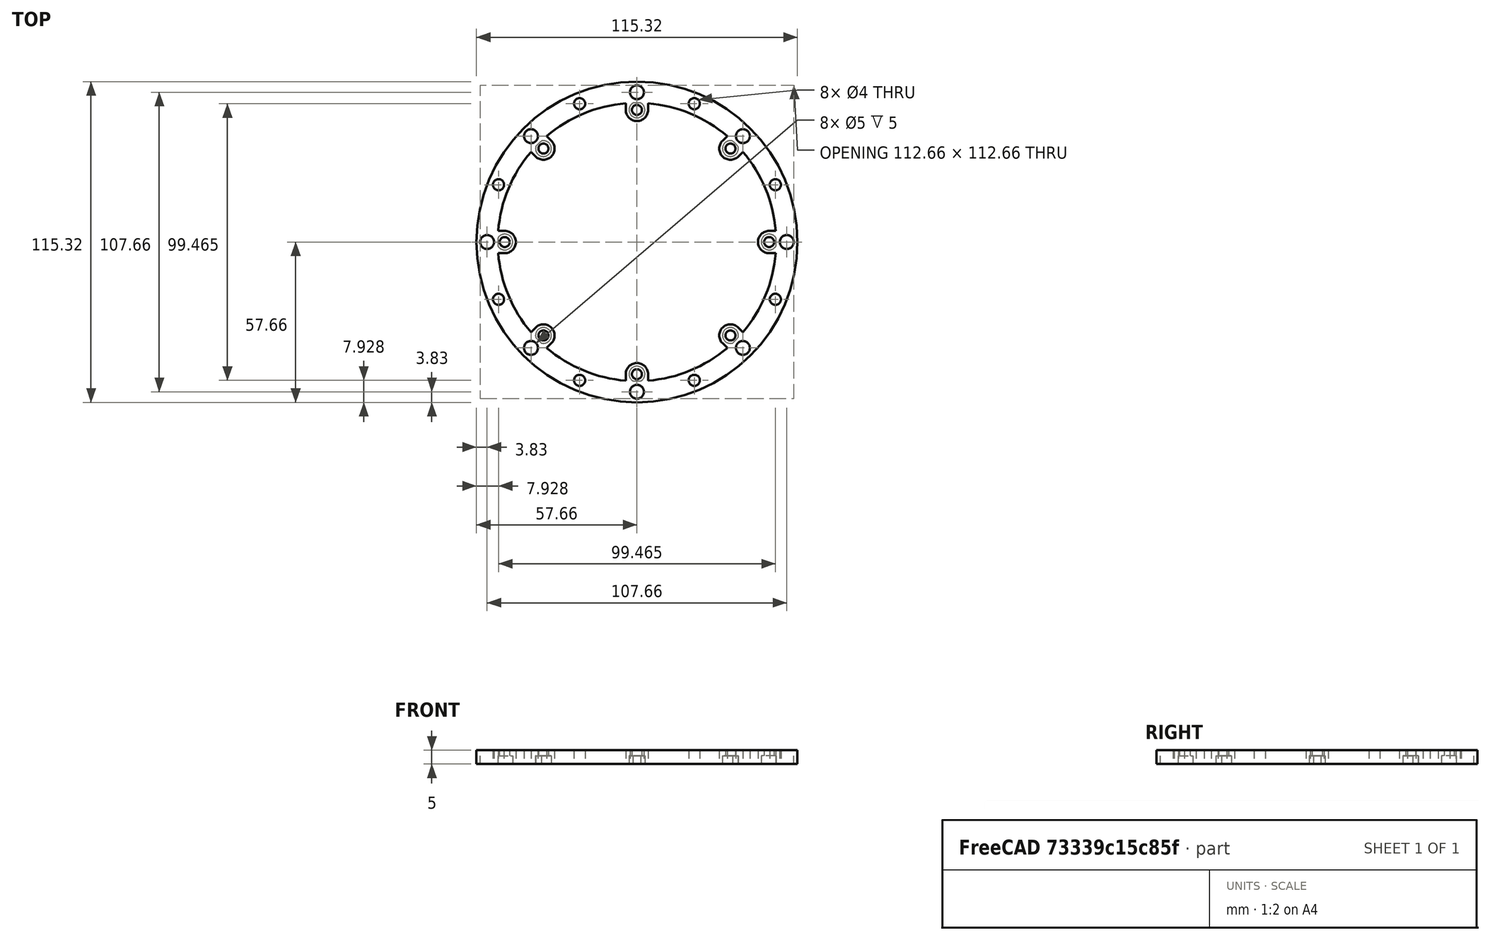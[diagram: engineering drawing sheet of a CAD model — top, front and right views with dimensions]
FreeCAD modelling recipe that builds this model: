
FCSTD DOCUMENT  (FreeCAD 0.20R)
Label: XL30ColumnAttachmentRing01
License: All rights reserved
LicenseURL: http://en.wikipedia.org/wiki/All_rights_reserved
objects: Part::Cylinder×34, TechDraw::DrawViewDimension×19, Part::Compound×18, Part::MultiFuse×17, Part::Cut×11, Part::Box×8, Part::FeaturePython×8, TechDraw::DrawProjGroupItem×2, Spreadsheet::Sheet×1, TechDraw::DrawSVGTemplate×1, TechDraw::DrawProjGroup×1, TechDraw::DrawViewSection×1, TechDraw::DrawViewAnnotation×1, TechDraw::DrawPage×1
note: 96 computed .brp shape members not serialized (recipe doc carries the construction recipe); baked Part::Feature solids carry a one-line shape summary decoded from their .brp

FEATURE [Spreadsheet::Sheet] Spreadsheet  label="AttachmentRing01"
  cells = A1=Ring configuration; A2=Inside diameter; B2(ring_id)=100; C2=Inside diameter of the column / poleshoe; E2=Ring width; F2(ring_width)==ring_od - ring_id; A3=Outside diameter; B3(ring_od)==100 + 2 * 7.66; C3=Outside diameter; A4=Thickness; B4(ring_thickness)=5; C4=Thickness of the mounting rin; A5=Thickness below mountscrew; B5(thickness_m3_below)=2
FEATURE [Part::Cylinder] Cylinder
  Angle = 360
  AttacherType = Attacher::AttachEngine3D
  FirstAngle = 0
  Height = 5
  Radius = 57.66
  SecondAngle = 0
  expr: Height = <<AttachmentRing01>>.ring_thickness
  expr: Radius = <<AttachmentRing01>>.ring_od / 2
FEATURE [Part::Cylinder] Cylinder001
  Angle = 360
  AttacherType = Attacher::AttachEngine3D
  FirstAngle = 0
  Height = 5
  Radius = 50
  SecondAngle = 0
  expr: Height = <<AttachmentRing01>>.ring_thickness
  expr: Radius = <<AttachmentRing01>>.ring_id / 2
FEATURE [Part::Cut] Cut
  Base = -> Cylinder
  Tool = -> Cylinder001
FEATURE [Part::Box] Box007  label="Cube007"
  AttacherType = Attacher::AttachEngine3D
  Height = 5
  Length = 4
  Placement = pos=(47.5,-4,0) rot=(0,0,1;0rad)
  Width = 8
  expr: Height = <<AttachmentRing01>>.ring_thickness
FEATURE [Part::Cylinder] Cylinder009
  Angle = 360
  AttacherType = Attacher::AttachEngine3D
  FirstAngle = 0
  Height = 5
  Placement = pos=(47.5,0,0) rot=(0,0,1;0rad)
  Radius = 4
  SecondAngle = 0
  expr: Height = <<AttachmentRing01>>.ring_thickness
FEATURE [Part::MultiFuse] Fusion008
  Shapes = -> [Cylinder009,Box007]
FEATURE [Part::Cylinder] Cylinder011
  Angle = 360
  AttacherType = Attacher::AttachEngine3D
  FirstAngle = 0
  Height = 10
  Placement = pos=(47.5,0,0) rot=(0,0,1;0rad)
  Radius = 1.8
  SecondAngle = 0
FEATURE [Part::Cylinder] Cylinder012
  Angle = 360
  AttacherType = Attacher::AttachEngine3D
  FirstAngle = 0
  Height = 3
  Placement = pos=(47.5,0,0) rot=(0,0,1;0rad)
  Radius = 2.84
  SecondAngle = 0
  expr: Height = <<AttachmentRing01>>.ring_thickness - <<AttachmentRing01>>.thickness_m3_below
FEATURE [Part::MultiFuse] Fusion
  Shapes = -> [Cylinder012,Cylinder011]
FEATURE [Part::Cut] Cut001
  Base = -> Fusion008
  Tool = -> Fusion
FEATURE [Part::Box] Box008  label="Cube008"
  AttacherType = Attacher::AttachEngine3D
  Height = 5
  Length = 4
  Placement = pos=(47.5,-4,0) rot=(0,0,1;0rad)
  Width = 8
  expr: Height = <<AttachmentRing01>>.ring_thickness
FEATURE [Part::Cylinder] Cylinder013
  Angle = 360
  AttacherType = Attacher::AttachEngine3D
  FirstAngle = 0
  Height = 5
  Placement = pos=(47.5,0,0) rot=(0,0,1;0rad)
  Radius = 4
  SecondAngle = 0
  expr: Height = <<AttachmentRing01>>.ring_thickness
FEATURE [Part::Cylinder] Cylinder014
  Angle = 360
  AttacherType = Attacher::AttachEngine3D
  FirstAngle = 0
  Height = 10
  Placement = pos=(47.5,0,0) rot=(0,0,1;0rad)
  Radius = 1.8
  SecondAngle = 0
FEATURE [Part::Cylinder] Cylinder015
  Angle = 360
  AttacherType = Attacher::AttachEngine3D
  FirstAngle = 0
  Height = 3
  Placement = pos=(47.5,0,0) rot=(0,0,1;0rad)
  Radius = 2.84
  SecondAngle = 0
  expr: Height = <<AttachmentRing01>>.ring_thickness - <<AttachmentRing01>>.thickness_m3_below
FEATURE [Part::MultiFuse] Fusion009
  Shapes = -> [Cylinder015,Cylinder014]
FEATURE [Part::MultiFuse] Fusion010
  Shapes = -> [Cylinder013,Box008]
FEATURE [Part::Cut] Cut002
  Base = -> Fusion010
  Placement = pos=(0,0,0) rot=(0,0,1;0.785398rad)
  Tool = -> Fusion009
FEATURE [Part::Box] Box009  label="Cube009"
  AttacherType = Attacher::AttachEngine3D
  Height = 5
  Length = 4
  Placement = pos=(47.5,-4,0) rot=(0,0,1;0rad)
  Width = 8
  expr: Height = <<AttachmentRing01>>.ring_thickness
FEATURE [Part::Cylinder] Cylinder016
  Angle = 360
  AttacherType = Attacher::AttachEngine3D
  FirstAngle = 0
  Height = 5
  Placement = pos=(47.5,0,0) rot=(0,0,1;0rad)
  Radius = 4
  SecondAngle = 0
  expr: Height = <<AttachmentRing01>>.ring_thickness
FEATURE [Part::Cylinder] Cylinder017
  Angle = 360
  AttacherType = Attacher::AttachEngine3D
  FirstAngle = 0
  Height = 10
  Placement = pos=(47.5,0,0) rot=(0,0,1;0rad)
  Radius = 1.8
  SecondAngle = 0
FEATURE [Part::Cylinder] Cylinder018
  Angle = 360
  AttacherType = Attacher::AttachEngine3D
  FirstAngle = 0
  Height = 3
  Placement = pos=(47.5,0,0) rot=(0,0,1;0rad)
  Radius = 2.84
  SecondAngle = 0
  expr: Height = <<AttachmentRing01>>.ring_thickness - <<AttachmentRing01>>.thickness_m3_below
FEATURE [Part::MultiFuse] Fusion011
  Shapes = -> [Cylinder018,Cylinder017]
FEATURE [Part::MultiFuse] Fusion012
  Shapes = -> [Cylinder016,Box009]
FEATURE [Part::Cut] Cut003
  Base = -> Fusion012
  Placement = pos=(0,0,0) rot=(0,0,1;1.5708rad)
  Tool = -> Fusion011
FEATURE [Part::Box] Box010  label="Cube010"
  AttacherType = Attacher::AttachEngine3D
  Height = 5
  Length = 4
  Placement = pos=(47.5,-4,0) rot=(0,0,1;0rad)
  Width = 8
  expr: Height = <<AttachmentRing01>>.ring_thickness
FEATURE [Part::Cylinder] Cylinder019
  Angle = 360
  AttacherType = Attacher::AttachEngine3D
  FirstAngle = 0
  Height = 5
  Placement = pos=(47.5,0,0) rot=(0,0,1;0rad)
  Radius = 4
  SecondAngle = 0
  expr: Height = <<AttachmentRing01>>.ring_thickness
FEATURE [Part::Cylinder] Cylinder020
  Angle = 360
  AttacherType = Attacher::AttachEngine3D
  FirstAngle = 0
  Height = 10
  Placement = pos=(47.5,0,0) rot=(0,0,1;0rad)
  Radius = 1.8
  SecondAngle = 0
FEATURE [Part::Cylinder] Cylinder021
  Angle = 360
  AttacherType = Attacher::AttachEngine3D
  FirstAngle = 0
  Height = 3
  Placement = pos=(47.5,0,0) rot=(0,0,1;0rad)
  Radius = 2.84
  SecondAngle = 0
  expr: Height = <<AttachmentRing01>>.ring_thickness - <<AttachmentRing01>>.thickness_m3_below
FEATURE [Part::MultiFuse] Fusion013
  Shapes = -> [Cylinder021,Cylinder020]
FEATURE [Part::MultiFuse] Fusion014
  Shapes = -> [Cylinder019,Box010]
FEATURE [Part::Cut] Cut004
  Base = -> Fusion014
  Placement = pos=(0,0,0) rot=(0,0,1;2.35619rad)
  Tool = -> Fusion013
FEATURE [Part::Box] Box011  label="Cube011"
  AttacherType = Attacher::AttachEngine3D
  Height = 5
  Length = 4
  Placement = pos=(47.5,-4,0) rot=(0,0,1;0rad)
  Width = 8
  expr: Height = <<AttachmentRing01>>.ring_thickness
FEATURE [Part::Cylinder] Cylinder022
  Angle = 360
  AttacherType = Attacher::AttachEngine3D
  FirstAngle = 0
  Height = 5
  Placement = pos=(47.5,0,0) rot=(0,0,1;0rad)
  Radius = 4
  SecondAngle = 0
  expr: Height = <<AttachmentRing01>>.ring_thickness
FEATURE [Part::Cylinder] Cylinder023
  Angle = 360
  AttacherType = Attacher::AttachEngine3D
  FirstAngle = 0
  Height = 10
  Placement = pos=(47.5,0,0) rot=(0,0,1;0rad)
  Radius = 1.8
  SecondAngle = 0
FEATURE [Part::Cylinder] Cylinder024
  Angle = 360
  AttacherType = Attacher::AttachEngine3D
  FirstAngle = 0
  Height = 3
  Placement = pos=(47.5,0,0) rot=(0,0,1;0rad)
  Radius = 2.84
  SecondAngle = 0
  expr: Height = <<AttachmentRing01>>.ring_thickness - <<AttachmentRing01>>.thickness_m3_below
FEATURE [Part::MultiFuse] Fusion015
  Shapes = -> [Cylinder024,Cylinder023]
FEATURE [Part::MultiFuse] Fusion016
  Shapes = -> [Cylinder022,Box011]
FEATURE [Part::Cut] Cut005
  Base = -> Fusion016
  Placement = pos=(0,0,0) rot=(0,0,1;3.14159rad)
  Tool = -> Fusion015
FEATURE [Part::Box] Box012  label="Cube012"
  AttacherType = Attacher::AttachEngine3D
  Height = 5
  Length = 4
  Placement = pos=(47.5,-4,0) rot=(0,0,1;0rad)
  Width = 8
  expr: Height = <<AttachmentRing01>>.ring_thickness
FEATURE [Part::Cylinder] Cylinder025
  Angle = 360
  AttacherType = Attacher::AttachEngine3D
  FirstAngle = 0
  Height = 5
  Placement = pos=(47.5,0,0) rot=(0,0,1;0rad)
  Radius = 4
  SecondAngle = 0
  expr: Height = <<AttachmentRing01>>.ring_thickness
FEATURE [Part::Cylinder] Cylinder026
  Angle = 360
  AttacherType = Attacher::AttachEngine3D
  FirstAngle = 0
  Height = 10
  Placement = pos=(47.5,0,0) rot=(0,0,1;0rad)
  Radius = 1.8
  SecondAngle = 0
FEATURE [Part::Cylinder] Cylinder027
  Angle = 360
  AttacherType = Attacher::AttachEngine3D
  FirstAngle = 0
  Height = 3
  Placement = pos=(47.5,0,0) rot=(0,0,1;0rad)
  Radius = 2.84
  SecondAngle = 0
  expr: Height = <<AttachmentRing01>>.ring_thickness - <<AttachmentRing01>>.thickness_m3_below
FEATURE [Part::MultiFuse] Fusion017
  Shapes = -> [Cylinder027,Cylinder026]
FEATURE [Part::MultiFuse] Fusion018
  Shapes = -> [Cylinder025,Box012]
FEATURE [Part::Cut] Cut006
  Base = -> Fusion018
  Placement = pos=(0,0,0) rot=(0,0,1;3.92699rad)
  Tool = -> Fusion017
FEATURE [Part::Box] Box013  label="Cube013"
  AttacherType = Attacher::AttachEngine3D
  Height = 5
  Length = 4
  Placement = pos=(47.5,-4,0) rot=(0,0,1;0rad)
  Width = 8
  expr: Height = <<AttachmentRing01>>.ring_thickness
FEATURE [Part::Cylinder] Cylinder028
  Angle = 360
  AttacherType = Attacher::AttachEngine3D
  FirstAngle = 0
  Height = 5
  Placement = pos=(47.5,0,0) rot=(0,0,1;0rad)
  Radius = 4
  SecondAngle = 0
  expr: Height = <<AttachmentRing01>>.ring_thickness
FEATURE [Part::Cylinder] Cylinder029
  Angle = 360
  AttacherType = Attacher::AttachEngine3D
  FirstAngle = 0
  Height = 10
  Placement = pos=(47.5,0,0) rot=(0,0,1;0rad)
  Radius = 1.8
  SecondAngle = 0
FEATURE [Part::Cylinder] Cylinder030
  Angle = 360
  AttacherType = Attacher::AttachEngine3D
  FirstAngle = 0
  Height = 3
  Placement = pos=(47.5,0,0) rot=(0,0,1;0rad)
  Radius = 2.84
  SecondAngle = 0
  expr: Height = <<AttachmentRing01>>.ring_thickness - <<AttachmentRing01>>.thickness_m3_below
FEATURE [Part::MultiFuse] Fusion019
  Shapes = -> [Cylinder030,Cylinder029]
FEATURE [Part::MultiFuse] Fusion020
  Shapes = -> [Cylinder028,Box013]
FEATURE [Part::Cut] Cut007
  Base = -> Fusion020
  Placement = pos=(0,0,0) rot=(0,0,1;4.71239rad)
  Tool = -> Fusion019
FEATURE [Part::Box] Box014  label="Cube014"
  AttacherType = Attacher::AttachEngine3D
  Height = 5
  Length = 4
  Placement = pos=(47.5,-4,0) rot=(0,0,1;0rad)
  Width = 8
  expr: Height = <<AttachmentRing01>>.ring_thickness
FEATURE [Part::Cylinder] Cylinder031
  Angle = 360
  AttacherType = Attacher::AttachEngine3D
  FirstAngle = 0
  Height = 5
  Placement = pos=(47.5,0,0) rot=(0,0,1;0rad)
  Radius = 4
  SecondAngle = 0
  expr: Height = <<AttachmentRing01>>.ring_thickness
FEATURE [Part::Cylinder] Cylinder032
  Angle = 360
  AttacherType = Attacher::AttachEngine3D
  FirstAngle = 0
  Height = 10
  Placement = pos=(47.5,0,0) rot=(0,0,1;0rad)
  Radius = 1.8
  SecondAngle = 0
FEATURE [Part::Cylinder] Cylinder033
  Angle = 360
  AttacherType = Attacher::AttachEngine3D
  FirstAngle = 0
  Height = 3
  Placement = pos=(47.5,0,0) rot=(0,0,1;0rad)
  Radius = 2.84
  SecondAngle = 0
  expr: Height = <<AttachmentRing01>>.ring_thickness - <<AttachmentRing01>>.thickness_m3_below
FEATURE [Part::MultiFuse] Fusion021
  Shapes = -> [Cylinder033,Cylinder032]
FEATURE [Part::MultiFuse] Fusion022
  Shapes = -> [Cylinder031,Box014]
FEATURE [Part::Cut] Cut008
  Base = -> Fusion022
  Placement = pos=(0,0,0) rot=(0,0,1;5.49779rad)
  Tool = -> Fusion021
FEATURE [Part::MultiFuse] Fusion023
  Shapes = -> [Cut,Cut001,Cut002,Cut003,Cut004,Cut005,Cut006,Cut007,Cut008]
FEATURE [Part::FeaturePython] Screw  label="M4x7-Screw001"  # Fasteners workbench fastener (typed FeaturePython)
  Placement = pos=(53.83,0,3.82) rot=(0,0,1;0rad)
  diameter = 5
  invert = false
  leftHanded = false
  length = 11
  lengthCustom = 7
  matchOuter = false
  offset = 0
  thread = false
  type = 48
  expr: .Placement.Base.x = (<<AttachmentRing01>>.ring_od + <<AttachmentRing01>>.ring_id) / 4
  expr: lengthCustom = <<AttachmentRing01>>.ring_thickness + 2
FEATURE [Part::Compound] Compound
  Links = -> [Screw]
  Placement = pos=(0,0,0) rot=(0,0,1;0.392699rad)
FEATURE [Part::FeaturePython] Screw001  label="M4x7-Screw002"  # Fasteners workbench fastener (typed FeaturePython)
  Placement = pos=(53.83,0,3.82) rot=(0,0,1;0rad)
  diameter = 5
  invert = false
  leftHanded = false
  length = 11
  lengthCustom = 7
  matchOuter = false
  offset = 0
  thread = false
  type = 48
  expr: .Placement.Base.x = (<<AttachmentRing01>>.ring_od + <<AttachmentRing01>>.ring_id) / 4
  expr: lengthCustom = <<AttachmentRing01>>.ring_thickness + 2
FEATURE [Part::Compound] Compound001
  Links = -> [Screw001]
  Placement = pos=(0,0,0) rot=(0,0,1;1.1781rad)
FEATURE [Part::FeaturePython] Screw002  label="M4x7-Screw003"  # Fasteners workbench fastener (typed FeaturePython)
  Placement = pos=(53.83,0,3.82) rot=(0,0,1;0rad)
  diameter = 5
  invert = false
  leftHanded = false
  length = 11
  lengthCustom = 7
  matchOuter = false
  offset = 0
  thread = false
  type = 48
  expr: .Placement.Base.x = (<<AttachmentRing01>>.ring_od + <<AttachmentRing01>>.ring_id) / 4
  expr: lengthCustom = <<AttachmentRing01>>.ring_thickness + 2
FEATURE [Part::Compound] Compound002
  Links = -> [Screw002]
  Placement = pos=(0,0,0) rot=(0,0,1;1.96349rad)
FEATURE [Part::FeaturePython] Screw003  label="M4x7-Screw004"  # Fasteners workbench fastener (typed FeaturePython)
  Placement = pos=(53.83,0,3.82) rot=(0,0,1;0rad)
  diameter = 5
  invert = false
  leftHanded = false
  length = 11
  lengthCustom = 7
  matchOuter = false
  offset = 0
  thread = false
  type = 48
  expr: .Placement.Base.x = (<<AttachmentRing01>>.ring_od + <<AttachmentRing01>>.ring_id) / 4
  expr: lengthCustom = <<AttachmentRing01>>.ring_thickness + 2
FEATURE [Part::Compound] Compound003
  Links = -> [Screw003]
  Placement = pos=(0,0,0) rot=(0,0,1;2.74889rad)
FEATURE [Part::FeaturePython] Screw004  label="M4x7-Screw005"  # Fasteners workbench fastener (typed FeaturePython)
  Placement = pos=(53.83,0,3.82) rot=(0,0,1;0rad)
  diameter = 5
  invert = false
  leftHanded = false
  length = 11
  lengthCustom = 7
  matchOuter = false
  offset = 0
  thread = false
  type = 48
  expr: .Placement.Base.x = (<<AttachmentRing01>>.ring_od + <<AttachmentRing01>>.ring_id) / 4
  expr: lengthCustom = <<AttachmentRing01>>.ring_thickness + 2
FEATURE [Part::Compound] Compound004
  Links = -> [Screw004]
  Placement = pos=(0,0,0) rot=(0,0,1;3.53429rad)
FEATURE [Part::FeaturePython] Screw005  label="M4x7-Screw006"  # Fasteners workbench fastener (typed FeaturePython)
  Placement = pos=(53.83,0,3.82) rot=(0,0,1;0rad)
  diameter = 5
  invert = false
  leftHanded = false
  length = 11
  lengthCustom = 7
  matchOuter = false
  offset = 0
  thread = false
  type = 48
  expr: .Placement.Base.x = (<<AttachmentRing01>>.ring_od + <<AttachmentRing01>>.ring_id) / 4
  expr: lengthCustom = <<AttachmentRing01>>.ring_thickness + 2
FEATURE [Part::Compound] Compound005
  Links = -> [Screw005]
  Placement = pos=(0,0,0) rot=(0,0,1;4.31969rad)
FEATURE [Part::FeaturePython] Screw006  label="M4x7-Screw007"  # Fasteners workbench fastener (typed FeaturePython)
  Placement = pos=(53.83,0,3.82) rot=(0,0,1;0rad)
  diameter = 5
  invert = false
  leftHanded = false
  length = 11
  lengthCustom = 7
  matchOuter = false
  offset = 0
  thread = false
  type = 48
  expr: .Placement.Base.x = (<<AttachmentRing01>>.ring_od + <<AttachmentRing01>>.ring_id) / 4
  expr: lengthCustom = <<AttachmentRing01>>.ring_thickness + 2
FEATURE [Part::Compound] Compound006
  Links = -> [Screw006]
  Placement = pos=(0,0,0) rot=(0,0,1;5.10509rad)
FEATURE [Part::FeaturePython] Screw007  label="M4x7-Screw"  # Fasteners workbench fastener (typed FeaturePython)
  Placement = pos=(53.83,0,3.82) rot=(0,0,1;0rad)
  diameter = 5
  invert = false
  leftHanded = false
  length = 11
  lengthCustom = 7
  matchOuter = false
  offset = 0
  thread = false
  type = 48
  expr: .Placement.Base.x = (<<AttachmentRing01>>.ring_od + <<AttachmentRing01>>.ring_id) / 4
  expr: lengthCustom = <<AttachmentRing01>>.ring_thickness + 2
FEATURE [Part::Compound] Compound007
  Links = -> [Screw007]
  Placement = pos=(0,0,0) rot=(0,0,1;5.89049rad)
FEATURE [Part::Compound] Compound008  label="M4Threadsx8"
  Links = -> [Compound007,Compound,Compound001,Compound002,Compound003,Compound004,Compound005,Compound006]
  Placement = pos=(0,0,2) rot=(0,0,1;0rad)
FEATURE [Part::Cut] Cut009
  Base = -> Fusion023
  Tool = -> Compound008
FEATURE [Part::Cylinder] Cylinder035
  Angle = 360
  AttacherType = Attacher::AttachEngine3D
  FirstAngle = 0
  Height = 5
  Placement = pos=(53.83,0,0) rot=(0,0,1;0rad)
  Radius = 2.5
  SecondAngle = 0
  expr: .Placement.Base.x = (<<AttachmentRing01>>.ring_od + <<AttachmentRing01>>.ring_id) / 4
  expr: Height = <<AttachmentRing01>>.ring_thickness
FEATURE [Part::Compound] Compound009
  Links = -> [Cylinder035]
FEATURE [Part::Cylinder] Cylinder036
  Angle = 360
  AttacherType = Attacher::AttachEngine3D
  FirstAngle = 0
  Height = 5
  Placement = pos=(53.83,0,0) rot=(0,0,1;0rad)
  Radius = 2.5
  SecondAngle = 0
  expr: .Placement.Base.x = (<<AttachmentRing01>>.ring_od + <<AttachmentRing01>>.ring_id) / 4
  expr: Height = <<AttachmentRing01>>.ring_thickness
FEATURE [Part::Compound] Compound010
  Links = -> [Cylinder036]
  Placement = pos=(0,0,0) rot=(0,0,1;0.785398rad)
FEATURE [Part::Cylinder] Cylinder037
  Angle = 360
  AttacherType = Attacher::AttachEngine3D
  FirstAngle = 0
  Height = 5
  Placement = pos=(53.83,0,0) rot=(0,0,1;0rad)
  Radius = 2.5
  SecondAngle = 0
  expr: .Placement.Base.x = (<<AttachmentRing01>>.ring_od + <<AttachmentRing01>>.ring_id) / 4
  expr: Height = <<AttachmentRing01>>.ring_thickness
FEATURE [Part::Compound] Compound011
  Links = -> [Cylinder037]
  Placement = pos=(0,0,0) rot=(0,0,1;1.5708rad)
FEATURE [Part::Cylinder] Cylinder038
  Angle = 360
  AttacherType = Attacher::AttachEngine3D
  FirstAngle = 0
  Height = 5
  Placement = pos=(53.83,0,0) rot=(0,0,1;0rad)
  Radius = 2.5
  SecondAngle = 0
  expr: .Placement.Base.x = (<<AttachmentRing01>>.ring_od + <<AttachmentRing01>>.ring_id) / 4
  expr: Height = <<AttachmentRing01>>.ring_thickness
FEATURE [Part::Compound] Compound012
  Links = -> [Cylinder038]
  Placement = pos=(0,0,0) rot=(0,0,1;2.35619rad)
FEATURE [Part::Cylinder] Cylinder039
  Angle = 360
  AttacherType = Attacher::AttachEngine3D
  FirstAngle = 0
  Height = 5
  Placement = pos=(53.83,0,0) rot=(0,0,1;0rad)
  Radius = 2.5
  SecondAngle = 0
  expr: .Placement.Base.x = (<<AttachmentRing01>>.ring_od + <<AttachmentRing01>>.ring_id) / 4
  expr: Height = <<AttachmentRing01>>.ring_thickness
FEATURE [Part::Compound] Compound013
  Links = -> [Cylinder039]
  Placement = pos=(0,0,0) rot=(0,0,1;3.14159rad)
FEATURE [Part::Cylinder] Cylinder040
  Angle = 360
  AttacherType = Attacher::AttachEngine3D
  FirstAngle = 0
  Height = 5
  Placement = pos=(53.83,0,0) rot=(0,0,1;0rad)
  Radius = 2.5
  SecondAngle = 0
  expr: .Placement.Base.x = (<<AttachmentRing01>>.ring_od + <<AttachmentRing01>>.ring_id) / 4
  expr: Height = <<AttachmentRing01>>.ring_thickness
FEATURE [Part::Compound] Compound014
  Links = -> [Cylinder040]
  Placement = pos=(0,0,0) rot=(0,0,1;3.92699rad)
FEATURE [Part::Cylinder] Cylinder041
  Angle = 360
  AttacherType = Attacher::AttachEngine3D
  FirstAngle = 0
  Height = 5
  Placement = pos=(53.83,0,0) rot=(0,0,1;0rad)
  Radius = 2.5
  SecondAngle = 0
  expr: .Placement.Base.x = (<<AttachmentRing01>>.ring_od + <<AttachmentRing01>>.ring_id) / 4
  expr: Height = <<AttachmentRing01>>.ring_thickness
FEATURE [Part::Compound] Compound015
  Links = -> [Cylinder041]
  Placement = pos=(0,0,0) rot=(0,0,1;4.71239rad)
FEATURE [Part::Cylinder] Cylinder042
  Angle = 360
  AttacherType = Attacher::AttachEngine3D
  FirstAngle = 0
  Height = 5
  Placement = pos=(53.83,0,0) rot=(0,0,1;0rad)
  Radius = 2.5
  SecondAngle = 0
  expr: .Placement.Base.x = (<<AttachmentRing01>>.ring_od + <<AttachmentRing01>>.ring_id) / 4
  expr: Height = <<AttachmentRing01>>.ring_thickness
FEATURE [Part::Compound] Compound016
  Links = -> [Cylinder042]
  Placement = pos=(0,0,0) rot=(0,0,1;5.49779rad)
FEATURE [Part::Compound] Compound017  label="LEDHoles"
  Links = -> [Compound016,Compound009,Compound010,Compound011,Compound012,Compound013,Compound014,Compound015]
FEATURE [Part::Cut] Cut010  label="AttachmentRing_Column01"
  Base = -> Cut009
  Tool = -> Compound017
FEATURE [TechDraw::DrawSVGTemplate] Template
  EditableTexts = Designed_by_Name=Thomas Spielauer; FC-Date=2023-11-15; FC-SC=mm; FC-SH=1/1; FC-Title=XL30 Column attachment ring; Subtitle=Compatible with XL30 ESEM
  Height = 210
  Orientation = 1
  Width = 297
FEATURE [TechDraw::DrawProjGroupItem] ProjItem  label="Front"
  CoarseView = false
  Direction = (0,0,1)
  Focus = 100
  HardHidden = false
  IsoCount = 0
  IsoHidden = false
  IsoVisible = false
  LockPosition = true
  Perspective = false
  Rotation = 0
  RotationVector = (-1,0,0)
  ScaleType = 2
  SeamHidden = false
  SeamVisible = true
  SmoothHidden = false
  SmoothVisible = true
  Source = -> [Cut010]
  Type = 0
  X = 0
  XDirection = (-1,0,0)
  Y = 0
FEATURE [TechDraw::DrawProjGroupItem] ProjItem001  label="Left"
  CoarseView = false
  Direction = (1,0,1e-16)
  Focus = 100
  HardHidden = false
  IsoCount = 0
  IsoHidden = false
  IsoVisible = false
  LockPosition = false
  Perspective = false
  Rotation = 0
  RotationVector = (1,0,0)
  ScaleType = 2
  SeamHidden = false
  SeamVisible = true
  SmoothHidden = false
  SmoothVisible = true
  Source = -> [Cut010]
  Type = 1
  X = 96.8512
  XDirection = (-1e-16,0,1)
  Y = 0
FEATURE [TechDraw::DrawProjGroup] ProjGroup
  Anchor = -> ProjItem
  AutoDistribute = true
  LockPosition = false
  ProjectionType = 0
  Rotation = 0
  ScaleType = 0
  Source = -> [Cut010]
  Views = -> [ProjItem,ProjItem001]
  X = 81.0853
  Y = 127.683
  spacingX = 15
  spacingY = 15
FEATURE [TechDraw::DrawViewDimension] Dimension
  AngleOverride = false
  Arbitrary = false
  ArbitraryTolerances = false
  EqualTolerance = true
  ExtensionAngle = 0
  FormatSpec = %.2w
  FormatSpecOverTolerance = %+.2w
  FormatSpecUnderTolerance = %+.2w
  Inverted = false
  LineAngle = 0
  LockPosition = false
  MeasureType = 1
  OverTolerance = 0
  References2D = -> [ProjItem001]
  Rotation = 0
  ScaleType = 0
  TheoreticalExact = false
  Type = 1
  UnderTolerance = 0
  X = 0
  Y = 69.5205
FEATURE [TechDraw::DrawViewDimension] Dimension001
  AngleOverride = false
  Arbitrary = false
  ArbitraryTolerances = false
  EqualTolerance = true
  ExtensionAngle = 0
  FormatSpec = %.2w
  FormatSpecOverTolerance = %+.2w
  FormatSpecUnderTolerance = %+.2w
  Inverted = false
  LineAngle = 0
  LockPosition = false
  MeasureType = 1
  OverTolerance = 0
  References2D = -> [ProjItem001]
  Rotation = 0
  ScaleType = 0
  TheoreticalExact = false
  Type = 2
  UnderTolerance = 0
  X = -13.7249
  Y = 2.5
FEATURE [TechDraw::DrawViewDimension] Dimension002
  AngleOverride = false
  Arbitrary = false
  ArbitraryTolerances = false
  EqualTolerance = true
  ExtensionAngle = 0
  FormatSpec = ⌀%.2w
  FormatSpecOverTolerance = %+.2w
  FormatSpecUnderTolerance = %+.2w
  Inverted = false
  LineAngle = 0
  LockPosition = false
  MeasureType = 1
  OverTolerance = 0
  References2D = -> [ProjItem]
  Rotation = 0
  ScaleType = 0
  TheoreticalExact = false
  Type = 5
  UnderTolerance = 0
  X = 26.0014
  Y = -5.98032
FEATURE [TechDraw::DrawViewDimension] Dimension003
  AngleOverride = false
  Arbitrary = false
  ArbitraryTolerances = false
  EqualTolerance = true
  ExtensionAngle = 0
  FormatSpec = ⌀%.2w
  FormatSpecOverTolerance = %+.2w
  FormatSpecUnderTolerance = %+.2w
  Inverted = false
  LineAngle = 0
  LockPosition = false
  MeasureType = 1
  OverTolerance = 0
  References2D = -> [ProjItem]
  Rotation = 0
  ScaleType = 0
  TheoreticalExact = false
  Type = 5
  UnderTolerance = 0
  X = 16.1209
  Y = 15.6008
FEATURE [TechDraw::DrawViewDimension] Dimension004
  AngleOverride = false
  Arbitrary = false
  ArbitraryTolerances = false
  EqualTolerance = true
  ExtensionAngle = 0
  FormatSpec = ⌀%.2w
  FormatSpecOverTolerance = %+.2w
  FormatSpecUnderTolerance = %+.2w
  Inverted = false
  LineAngle = 0
  LockPosition = false
  MeasureType = 1
  OverTolerance = 0
  References2D = -> [ProjItem]
  Rotation = 0
  ScaleType = 0
  TheoreticalExact = false
  Type = 5
  UnderTolerance = 0
  X = -15.3841
  Y = 32.9351
FEATURE [TechDraw::DrawViewDimension] Dimension005
  AngleOverride = false
  Arbitrary = false
  ArbitraryTolerances = false
  EqualTolerance = true
  ExtensionAngle = 0
  FormatSpec = ⌀%.2w (8x)
  FormatSpecOverTolerance = %+.2w
  FormatSpecUnderTolerance = %+.2w
  Inverted = false
  LineAngle = 0
  LockPosition = false
  MeasureType = 1
  OverTolerance = 0
  References2D = -> [ProjItem]
  Rotation = 0
  ScaleType = 0
  TheoreticalExact = false
  Type = 5
  UnderTolerance = 0
  X = 30.3179
  Y = 8.53362
FEATURE [TechDraw::DrawViewDimension] Dimension006
  AngleOverride = false
  Arbitrary = false
  ArbitraryTolerances = false
  EqualTolerance = true
  ExtensionAngle = 0
  FormatSpec = R%.2w
  FormatSpecOverTolerance = %+.2w
  FormatSpecUnderTolerance = %+.2w
  Inverted = false
  LineAngle = 0
  LockPosition = false
  MeasureType = 1
  OverTolerance = 0
  References2D = -> [ProjItem]
  Rotation = 0
  ScaleType = 0
  TheoreticalExact = false
  Type = 4
  UnderTolerance = 0
  X = 38.1692
  Y = -2.68491
FEATURE [TechDraw::DrawViewDimension] Dimension007
  AngleOverride = false
  Arbitrary = false
  ArbitraryTolerances = false
  EqualTolerance = true
  ExtensionAngle = 0
  FormatSpec = ⌀%.2w
  FormatSpecOverTolerance = %+.2w
  FormatSpecUnderTolerance = %+.2w
  Inverted = false
  LineAngle = 0
  LockPosition = false
  MeasureType = 1
  OverTolerance = 0
  References2D = -> [ProjItem]
  Rotation = 0
  ScaleType = 0
  TheoreticalExact = false
  Type = 5
  UnderTolerance = 0
  X = 5.93397
  Y = 35.3665
FEATURE [TechDraw::DrawViewDimension] Dimension008
  AngleOverride = false
  Arbitrary = false
  ArbitraryTolerances = false
  EqualTolerance = true
  ExtensionAngle = 0
  FormatSpec = ⌀%.2w (8x M4)
  FormatSpecOverTolerance = %+.2w
  FormatSpecUnderTolerance = %+.2w
  Inverted = false
  LineAngle = 0
  LockPosition = false
  MeasureType = 1
  OverTolerance = 0
  References2D = -> [ProjItem]
  Rotation = 0
  ScaleType = 0
  TheoreticalExact = false
  Type = 5
  UnderTolerance = 0
  X = 62.3067
  Y = 54.6321
FEATURE [TechDraw::DrawViewDimension] Dimension009
  AngleOverride = false
  Arbitrary = false
  ArbitraryTolerances = false
  EqualTolerance = true
  ExtensionAngle = 0
  FormatSpec = ⌀%.2w (8x)
  FormatSpecOverTolerance = %+.2w
  FormatSpecUnderTolerance = %+.2w
  Inverted = false
  LineAngle = 0
  LockPosition = false
  MeasureType = 1
  OverTolerance = 0
  References2D = -> [ProjItem]
  Rotation = 0
  ScaleType = 0
  TheoreticalExact = false
  Type = 5
  UnderTolerance = 0
  X = 67.2121
  Y = 43.1993
FEATURE [TechDraw::DrawViewDimension] Dimension010
  AngleOverride = false
  Arbitrary = false
  ArbitraryTolerances = false
  EqualTolerance = true
  ExtensionAngle = 0
  FormatSpec = %.2w
  FormatSpecOverTolerance = %+.2w
  FormatSpecUnderTolerance = %+.2w
  Inverted = false
  LineAngle = 0
  LockPosition = false
  MeasureType = 1
  OverTolerance = 0
  References2D = -> [ProjItem]
  Rotation = 0
  ScaleType = 0
  TheoreticalExact = false
  Type = 6
  UnderTolerance = 0
  X = -47.4718
  Y = 56.4914
FEATURE [TechDraw::DrawViewDimension] Dimension011
  AngleOverride = false
  Arbitrary = false
  ArbitraryTolerances = false
  EqualTolerance = true
  ExtensionAngle = 0
  FormatSpec = %.2w
  FormatSpecOverTolerance = %+.2w
  FormatSpecUnderTolerance = %+.2w
  Inverted = false
  LineAngle = 0
  LockPosition = false
  MeasureType = 1
  OverTolerance = 0
  References2D = -> [ProjItem]
  Rotation = 0
  ScaleType = 0
  TheoreticalExact = false
  Type = 2
  UnderTolerance = 0
  X = -40.7742
  Y = 10.0235
FEATURE [TechDraw::DrawViewDimension] Dimension012
  AngleOverride = false
  Arbitrary = false
  ArbitraryTolerances = false
  EqualTolerance = true
  ExtensionAngle = 0
  FormatSpec = %.2w
  FormatSpecOverTolerance = %+.2w
  FormatSpecUnderTolerance = %+.2w
  Inverted = false
  LineAngle = 0
  LockPosition = false
  MeasureType = 1
  OverTolerance = 0
  References2D = -> [ProjItem]
  Rotation = 0
  ScaleType = 0
  TheoreticalExact = false
  Type = 6
  UnderTolerance = 0
  X = -58.1529
  Y = 34.417
FEATURE [TechDraw::DrawViewDimension] Dimension013
  AngleOverride = false
  Arbitrary = false
  ArbitraryTolerances = false
  EqualTolerance = true
  ExtensionAngle = 0
  FormatSpec = %.2w
  FormatSpecOverTolerance = %+.2w
  FormatSpecUnderTolerance = %+.2w
  Inverted = false
  LineAngle = 0
  LockPosition = false
  MeasureType = 1
  OverTolerance = 0
  References2D = -> [ProjItem]
  Rotation = 0
  ScaleType = 0
  TheoreticalExact = false
  Type = 6
  UnderTolerance = 0
  X = 34.043
  Y = 60.293
FEATURE [TechDraw::DrawViewSection] SectionView  label="Section  - "
  BaseView = -> ProjItem
  CoarseView = false
  CutSurfaceDisplay = 2
  Direction = (0,-1,0)
  FileGeomPattern = <path>
  FileHatchPattern = <path>
  Focus = 100
  FuseBeforeCut = false
  HardHidden = false
  HatchScale = 1
  IsoCount = 0
  IsoHidden = false
  IsoVisible = false
  LockPosition = false
  NameGeomPattern = Diamond
  Perspective = false
  Rotation = 0
  ScaleType = 2
  SeamHidden = false
  SeamVisible = true
  SectionDirection = 3
  SectionNormal = (0,-1,0)
  SectionOrigin = (0.038,0,2.5)
  SmoothHidden = false
  SmoothVisible = true
  Source = -> [Cut010]
  X = 72.1219
  XDirection = (-1,0,0)
  Y = 40.7089
FEATURE [TechDraw::DrawViewDimension] Dimension014
  AngleOverride = false
  Arbitrary = false
  ArbitraryTolerances = false
  EqualTolerance = true
  ExtensionAngle = 0
  FormatSpec = %.2w
  FormatSpecOverTolerance = %+.2w
  FormatSpecUnderTolerance = %+.2w
  Inverted = false
  LineAngle = 0
  LockPosition = false
  MeasureType = 1
  OverTolerance = 0
  References2D = -> [SectionView]
  Rotation = 0
  ScaleType = 0
  TheoreticalExact = false
  Type = 2
  UnderTolerance = 0
  X = 64.9678
  Y = 16.8618
FEATURE [TechDraw::DrawViewDimension] Dimension015
  AngleOverride = false
  Arbitrary = false
  ArbitraryTolerances = false
  EqualTolerance = true
  ExtensionAngle = 0
  FormatSpec = %.2w
  FormatSpecOverTolerance = %+.2w
  FormatSpecUnderTolerance = %+.2w
  Inverted = false
  LineAngle = 0
  LockPosition = false
  MeasureType = 1
  OverTolerance = 0
  References2D = -> [SectionView]
  Rotation = 0
  ScaleType = 0
  TheoreticalExact = false
  Type = 2
  UnderTolerance = 0
  X = 58.8699
  Y = -9.8339
FEATURE [TechDraw::DrawViewDimension] Dimension016
  AngleOverride = false
  Arbitrary = false
  ArbitraryTolerances = false
  EqualTolerance = true
  ExtensionAngle = 0
  FormatSpec = %.2w
  FormatSpecOverTolerance = %+.2w
  FormatSpecUnderTolerance = %+.2w
  Inverted = false
  LineAngle = 0
  LockPosition = false
  MeasureType = 1
  OverTolerance = 0
  References2D = -> [SectionView]
  Rotation = 0
  ScaleType = 0
  TheoreticalExact = false
  Type = 1
  UnderTolerance = 0
  X = 37.6693
  Y = 16.2953
FEATURE [TechDraw::DrawViewDimension] Dimension017
  AngleOverride = false
  Arbitrary = false
  ArbitraryTolerances = false
  EqualTolerance = true
  ExtensionAngle = 0
  FormatSpec = %.2w
  FormatSpecOverTolerance = %+.2w
  FormatSpecUnderTolerance = %+.2w
  Inverted = false
  LineAngle = 0
  LockPosition = false
  MeasureType = 1
  OverTolerance = 0
  References2D = -> [SectionView]
  Rotation = 0
  ScaleType = 0
  TheoreticalExact = false
  Type = 1
  UnderTolerance = 0
  X = 37.9214
  Y = -3.99108
FEATURE [TechDraw::DrawViewDimension] Dimension018
  AngleOverride = false
  Arbitrary = false
  ArbitraryTolerances = false
  EqualTolerance = true
  ExtensionAngle = 0
  FormatSpec = %.2w
  FormatSpecOverTolerance = %+.2w
  FormatSpecUnderTolerance = %+.2w
  Inverted = false
  LineAngle = 0
  LockPosition = false
  MeasureType = 1
  OverTolerance = 0
  References2D = -> [SectionView]
  Rotation = 0
  ScaleType = 0
  TheoreticalExact = false
  Type = 1
  UnderTolerance = 0
  X = -44.6513
  Y = 15.5079
FEATURE [TechDraw::DrawViewAnnotation] Annotation
  Font = osifont
  LineSpace = 80
  LockPosition = false
  MaxWidth = -1
  Rotation = 0
  ScaleType = 0
  Text = Ring with: | * 8x 5mm through holes | * 8x M4 tapped holes | * 8x 3.6mm through holes for M3 |    DIN912 screw heads. |   (M3 screw heads sunken |   into the lugs)
  TextSize = 5
  TextStyle = 0
  X = 250.875
  Y = 168.492
FEATURE [TechDraw::DrawPage] Page
  KeepUpdated = true
  NextBalloonIndex = 1
  ProjectionType = 0
  Template = -> Template
  Views = -> [ProjGroup,Dimension,Dimension001,Dimension002,Dimension003,Dimension004,Dimension005,Dimension006,Dimension007,Dimension008,Dimension009,Dimension010,Dimension011,Dimension012,Dimension013,SectionView,Dimension014,Dimension015,Dimension016,Dimension017,Dimension018,Annotation]
note: 2 file-system paths scrubbed to <path> (originals preserved in the JSON sidecar)
